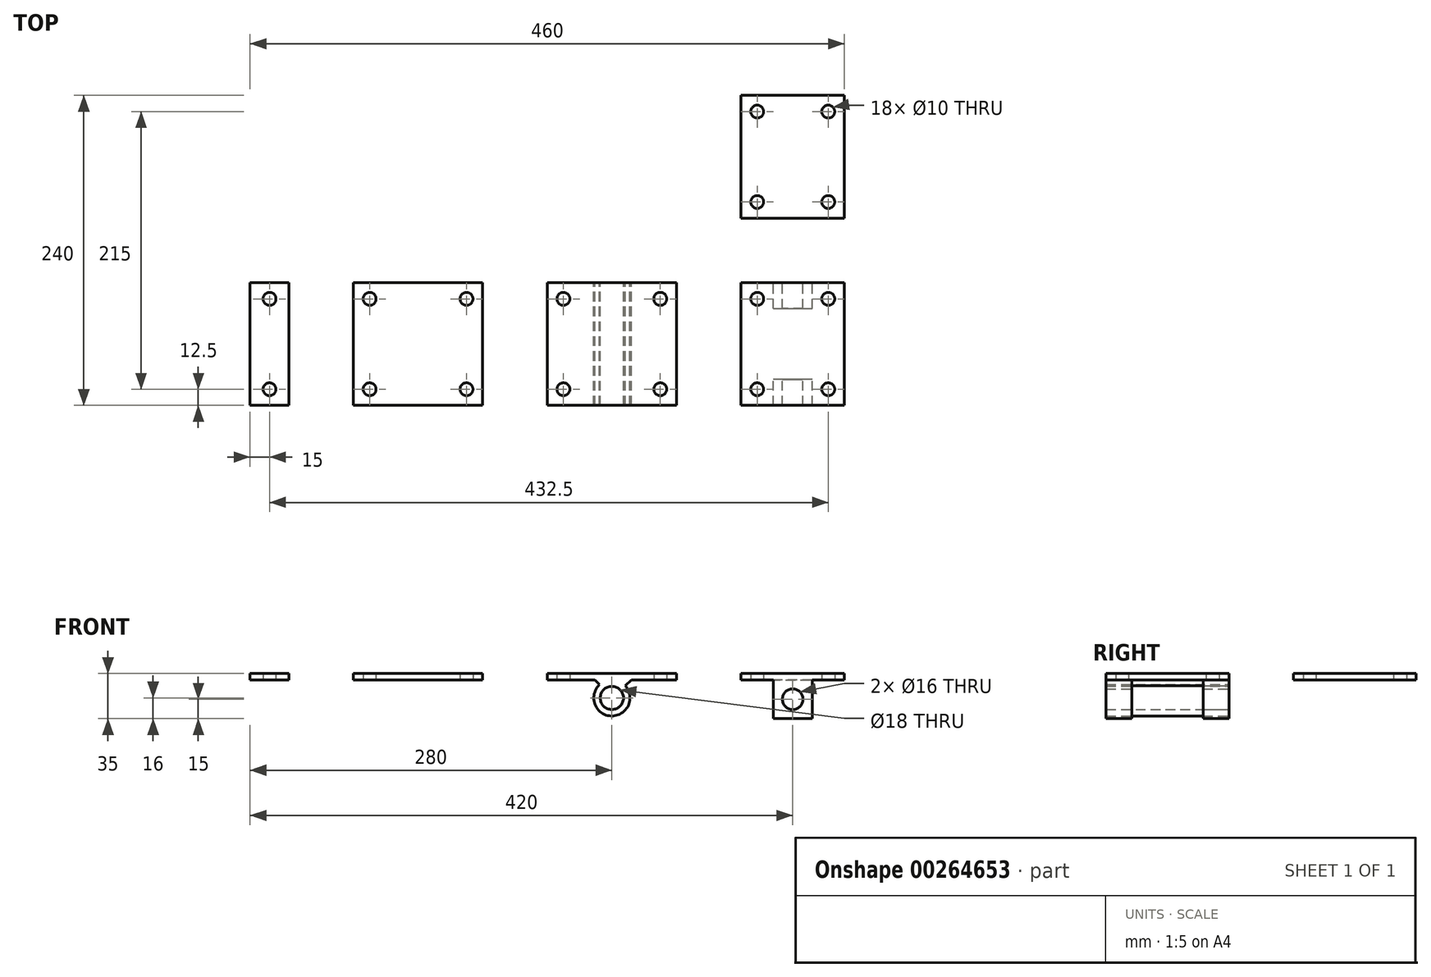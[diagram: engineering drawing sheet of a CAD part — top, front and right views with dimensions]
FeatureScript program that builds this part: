
annotation { "Feature Type Name" : "Feature", "Feature Type Description" : "" }
export const myFeature = defineFeature(function(context is Context, id is Id, definition is map)
    precondition{}
    {
        {
            var Q0;
            Q0=qCreatedBy(makeId("Top.planeOp"),FACE);
            var sketch = newSketch(context, id + "F0", { "sketchPlane" : qUnion([Q0])});
            skLineSegment(sketch, "E0", {"start": v(0, 0) * mm, "end": v(0, 47.5) * mm});
            skLineSegment(sketch, "E1", {"start": v(0, 47.5) * mm, "end": v(100, 47.5) * mm});
            skLineSegment(sketch, "E2", {"start": v(100, 47.5) * mm, "end": v(100, -47.5) * mm});
            skLineSegment(sketch, "E3", {"start": v(100, -47.5) * mm, "end": v(0, -47.5) * mm});
            skLineSegment(sketch, "E4", {"start": v(0, -47.5) * mm, "end": v(0, 0) * mm});
            skLineSegment(sketch, "E5", {"start": v(-50, 47.5) * mm, "end": v(-50, -47.5) * mm});
            skLineSegment(sketch, "E6", {"start": v(-50, -47.5) * mm, "end": v(-80, -47.5) * mm});
            skLineSegment(sketch, "E7", {"start": v(-80, -47.5) * mm, "end": v(-80, 47.5) * mm});
            skLineSegment(sketch, "E8", {"start": v(-80, 47.5) * mm, "end": v(-50, 47.5) * mm});
            skLineSegment(sketch, "E9", {"start": v(125, 47.5) * mm, "end": v(125, -47.5) * mm, "construction": true});
            skLineSegment(sketch, "E10.MirrorCS", {"start": v(150, -47.5) * mm, "end": v(250, -47.5) * mm});
            skLineSegment(sketch, "E11.MirrorCS", {"start": v(150, 47.5) * mm, "end": v(150, -47.5) * mm});
            skLineSegment(sketch, "E12.MirrorCS", {"start": v(250, 47.5) * mm, "end": v(150, 47.5) * mm});
            skLineSegment(sketch, "E13.MirrorCS", {"start": v(250, 0) * mm, "end": v(250, 47.5) * mm});
            skLineSegment(sketch, "E14.MirrorCS", {"start": v(250, -47.5) * mm, "end": v(250, 0) * mm});
            skLineSegment(sketch, "E15", {"start": v(300, 47.5) * mm, "end": v(300, -47.5) * mm});
            skLineSegment(sketch, "E16", {"start": v(300, -47.5) * mm, "end": v(380, -47.5) * mm});
            skLineSegment(sketch, "E17", {"start": v(380, -47.5) * mm, "end": v(380, 47.5) * mm});
            skLineSegment(sketch, "E18", {"start": v(380, 47.5) * mm, "end": v(300, 47.5) * mm});
            skLineSegment(sketch, "E19", {"start": v(300, 72.5) * mm, "end": v(380, 72.5) * mm, "construction": true});
            skLineSegment(sketch, "E20.MirrorCS", {"start": v(380, 192.5) * mm, "end": v(380, 97.5) * mm});
            skLineSegment(sketch, "E21.MirrorCS", {"start": v(380, 97.5) * mm, "end": v(300, 97.5) * mm});
            skLineSegment(sketch, "E22.MirrorCS", {"start": v(300, 97.5) * mm, "end": v(300, 192.5) * mm});
            skLineSegment(sketch, "E23.MirrorCS", {"start": v(300, 192.5) * mm, "end": v(380, 192.5) * mm});
            skLineSegment(sketch, "E24.0", {"start": v(87.5, 35) * mm, "end": v(87.5, -35) * mm, "construction": true});
            skLineSegment(sketch, "E24.1", {"start": v(12.5, 35) * mm, "end": v(87.5, 35) * mm, "construction": true});
            skLineSegment(sketch, "E24.2", {"start": v(87.5, -35) * mm, "end": v(12.5, -35) * mm, "construction": true});
            skLineSegment(sketch, "E24.3", {"start": v(12.5, -35) * mm, "end": v(12.5, 0) * mm, "construction": true});
            skLineSegment(sketch, "E24.4", {"start": v(12.5, 0) * mm, "end": v(12.5, 35) * mm, "construction": true});
            skCircle(sketch, "E25", {"center": v(12.5, 35) * mm, "radius": 5 * mm});
            skCircle(sketch, "E26", {"center": v(12.5, -35) * mm, "radius": 5 * mm});
            skCircle(sketch, "E27", {"center": v(87.5, -35) * mm, "radius": 5 * mm});
            skCircle(sketch, "E28", {"center": v(87.5, 35) * mm, "radius": 5 * mm});
            skLineSegment(sketch, "E29.0", {"start": v(-67.5, -35) * mm, "end": v(-67.5, 35) * mm, "construction": true});
            skLineSegment(sketch, "E29.1", {"start": v(-62.5, -35) * mm, "end": v(-67.5, -35) * mm, "construction": true});
            skLineSegment(sketch, "E29.2", {"start": v(-62.5, 35) * mm, "end": v(-62.5, -35) * mm, "construction": true});
            skLineSegment(sketch, "E29.3", {"start": v(-67.5, 35) * mm, "end": v(-62.5, 35) * mm, "construction": true});
            skCircle(sketch, "E30", {"center": v(-65, -35) * mm, "radius": 5 * mm});
            skCircle(sketch, "E31", {"center": v(-65, 35) * mm, "radius": 5 * mm});
            skLineSegment(sketch, "E32.0", {"start": v(162.5, 35) * mm, "end": v(162.5, -35) * mm, "construction": true});
            skLineSegment(sketch, "E32.1", {"start": v(237.5, 35) * mm, "end": v(162.5, 35) * mm, "construction": true});
            skLineSegment(sketch, "E32.2", {"start": v(162.5, -35) * mm, "end": v(237.5, -35) * mm, "construction": true});
            skLineSegment(sketch, "E32.3", {"start": v(237.5, -35) * mm, "end": v(237.5, 0) * mm, "construction": true});
            skLineSegment(sketch, "E32.4", {"start": v(237.5, 0) * mm, "end": v(237.5, 35) * mm, "construction": true});
            skCircle(sketch, "E33", {"center": v(162.5, 35) * mm, "radius": 5 * mm});
            skCircle(sketch, "E34", {"center": v(162.5, -35) * mm, "radius": 5 * mm});
            skCircle(sketch, "E35", {"center": v(237.5, -35) * mm, "radius": 5 * mm});
            skCircle(sketch, "E36", {"center": v(237.5, 35) * mm, "radius": 5 * mm});
            skLineSegment(sketch, "E37.0", {"start": v(367.5, 35) * mm, "end": v(312.5, 35) * mm, "construction": true});
            skLineSegment(sketch, "E37.1", {"start": v(367.5, -35) * mm, "end": v(367.5, 35) * mm, "construction": true});
            skLineSegment(sketch, "E37.2", {"start": v(312.5, -35) * mm, "end": v(367.5, -35) * mm, "construction": true});
            skLineSegment(sketch, "E37.3", {"start": v(312.5, 35) * mm, "end": v(312.5, -35) * mm, "construction": true});
            skCircle(sketch, "E38", {"center": v(312.5, 35) * mm, "radius": 5 * mm});
            skCircle(sketch, "E39", {"center": v(312.5, -35) * mm, "radius": 5 * mm});
            skCircle(sketch, "E40", {"center": v(367.5, -35) * mm, "radius": 5 * mm});
            skCircle(sketch, "E41", {"center": v(367.5, 35) * mm, "radius": 5 * mm});
            skLineSegment(sketch, "E42.0", {"start": v(312.5, 180) * mm, "end": v(367.5, 180) * mm, "construction": true});
            skLineSegment(sketch, "E42.1", {"start": v(312.5, 110) * mm, "end": v(312.5, 180) * mm, "construction": true});
            skLineSegment(sketch, "E42.2", {"start": v(367.5, 110) * mm, "end": v(312.5, 110) * mm, "construction": true});
            skLineSegment(sketch, "E42.3", {"start": v(367.5, 180) * mm, "end": v(367.5, 110) * mm, "construction": true});
            skCircle(sketch, "E43", {"center": v(312.5, 180) * mm, "radius": 5 * mm});
            skCircle(sketch, "E44", {"center": v(312.5, 110) * mm, "radius": 5 * mm});
            skCircle(sketch, "E45", {"center": v(367.5, 110) * mm, "radius": 5 * mm});
            skCircle(sketch, "E46", {"center": v(367.5, 180) * mm, "radius": 5 * mm});
            skSolve(sketch);
        }
        {
            var Q0;
            Q0 = qSketchRegion(id + "F0", true);
            extrude(context, id + "F1", {"entities" : qUnion([Q0]), "depth" : 5 * mm});
        }
        {
            var Q0;
            Q0=qCreatedBy(makeId("Front.planeOp"),FACE);
            var sketch = newSketch(context, id + "F2", { "sketchPlane" : qUnion([Q0])});
            skLineSegment(sketch, "E47.0.0", {"start": v(250, 0) * mm, "end": v(150, 0) * mm});
            skLineSegment(sketch, "E47.0.2", {"start": v(150, 0) * mm, "end": v(250, 0) * mm});
            skCircle(sketch, "E48", {"center": v(200, -14) * mm, "radius": 9 * mm});
            skCircle(sketch, "E49", {"center": v(200, -14) * mm, "radius": 14 * mm});
            skLineSegment(sketch, "E50", {"start": v(200, 0) * mm, "end": v(200, -14) * mm, "construction": true});
            skLineSegment(sketch, "E51", {"start": v(210.26, -4.47) * mm, "end": v(215.08, 0) * mm});
            skLineSegment(sketch, "E52", {"start": v(190.47, -3.74) * mm, "end": v(187, 0) * mm});
            skLineSegment(sketch, "E53.0.1", {"start": v(380, 0) * mm, "end": v(300, 0) * mm});
            skLineSegment(sketch, "E53.0.3", {"start": v(300, 0) * mm, "end": v(380, 0) * mm});
            skLineSegment(sketch, "E54", {"start": v(325, 0) * mm, "end": v(325, -30) * mm});
            skLineSegment(sketch, "E55", {"start": v(325, -30) * mm, "end": v(355, -30) * mm});
            skLineSegment(sketch, "E56", {"start": v(355, -30) * mm, "end": v(355, 0) * mm});
            skLineSegment(sketch, "E57", {"start": v(340, 0) * mm, "end": v(340, -30) * mm, "construction": true});
            skCircle(sketch, "E58", {"center": v(340, -15) * mm, "radius": 8 * mm});
            skSolve(sketch);
        }
        {
            var Q0;
            {var subQ0=sQuery(id+"F2.wireOp",EDGE,"E52");Q0=makeQuery(id+"F2.imprint","IMPRINT",FACE,{"disambiguationData":[TD([[makeQuery(id+"F2.imprint","IMPRINT",EDGE,{"derivedFrom":subQ0}),-1.0]])]});}
            var Q1;
            {var subQ0=sQuery(id+"F2.wireOp",EDGE,"E51");Q1=makeQuery(id+"F2.imprint","IMPRINT",FACE,{"disambiguationData":[TD([[makeQuery(id+"F2.imprint","IMPRINT",EDGE,{"derivedFrom":subQ0}),1.0]])]});}
            var Q2;
            Q2=makeQuery(id+"F2.imprint","IMPRINT",FACE,{"disambiguationData":[TD([[makeQuery(id+"F2.imprint","IMPRINT",EDGE,{"derivedFrom":sQuery(id+"F2.wireOp",EDGE,"E48")}),-1.0]])]});
            extrude(context, id + "F3", {"entities" : qUnion([Q0, Q1, Q2]), "operationType" : NewBodyOperationType.ADD, "endBound" : BoundingType.SYMMETRIC, "depth" : 95 * mm});
        }
        {
            var Q0;
            {var subQ1=sQuery(id+"F2.wireOp",EDGE,"E54");Q0=makeQuery(id+"F2.imprint","IMPRINT",FACE,{"disambiguationData":[TD([[makeQuery(id+"F2.imprint","IMPRINT",EDGE,{"derivedFrom":subQ1}),1.0]])]});}
            extrude(context, id + "F4", {"entities" : qUnion([Q0]), "operationType" : NewBodyOperationType.ADD, "endBound" : BoundingType.SYMMETRIC, "depth" : 95 * mm});
        }
        {
            var Q0;
            {var subQ1=sQuery(id+"F2.wireOp",EDGE,"E54");Q0=makeQuery(id+"F2.imprint","IMPRINT",FACE,{"disambiguationData":[TD([[makeQuery(id+"F2.imprint","IMPRINT",EDGE,{"derivedFrom":subQ1}),1.0]])]});}
            extrude(context, id + "F5", {"entities" : qUnion([Q0]), "operationType" : NewBodyOperationType.REMOVE, "endBound" : BoundingType.SYMMETRIC, "oppositeDirection" : true, "depth" : 55 * mm});
        }
    });
